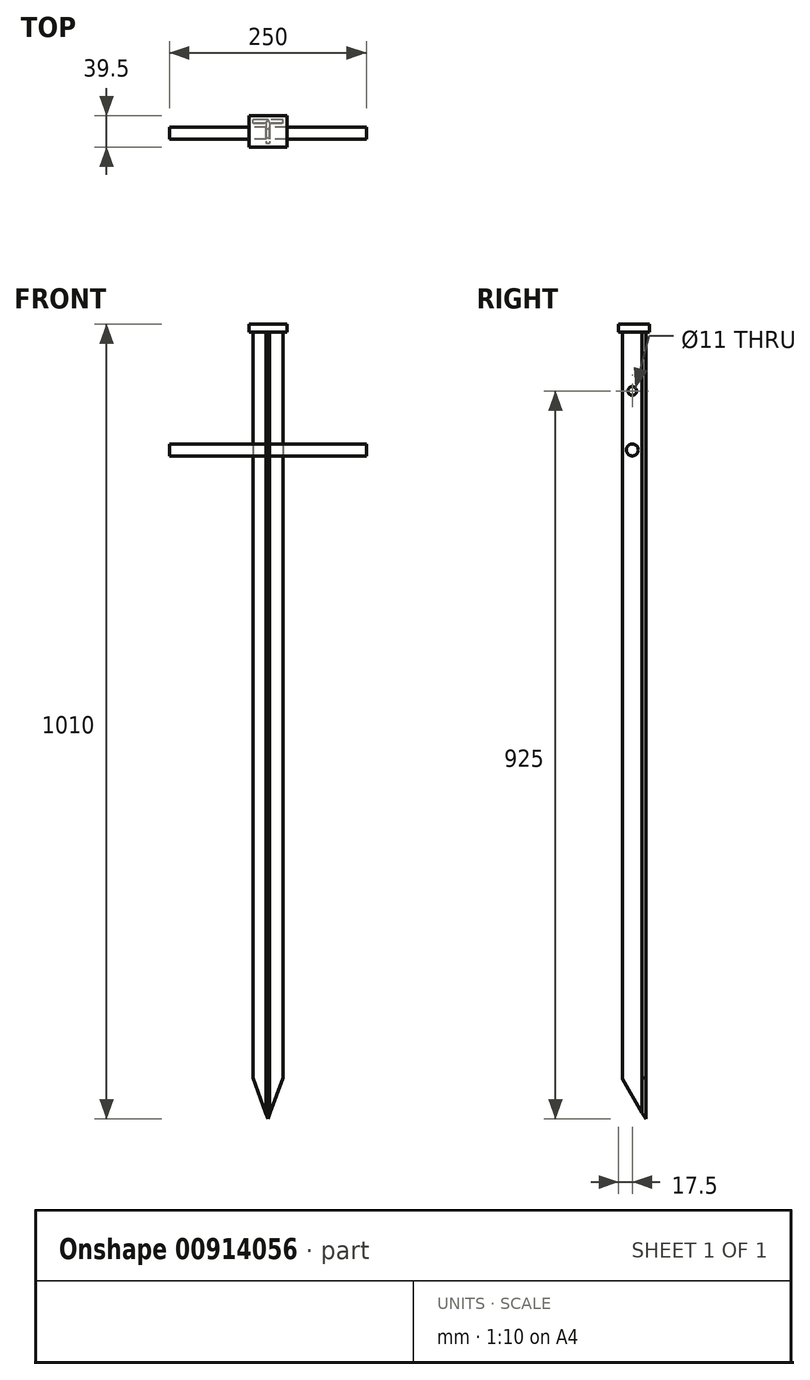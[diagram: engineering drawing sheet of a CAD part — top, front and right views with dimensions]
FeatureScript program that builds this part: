
annotation { "Feature Type Name" : "Feature", "Feature Type Description" : "" }
export const myFeature = defineFeature(function(context is Context, id is Id, definition is map)
    precondition{}
    {
        {
            var Q0;
            Q0=qCreatedBy(makeId("Top.planeOp"),FACE);
            var sketch = newSketch(context, id + "F0", { "sketchPlane" : qUnion([Q0])});
            skLineSegment(sketch, "E0.bottom", {"start": v(19, -2.25) * mm, "end": v(-19, -2.25) * mm});
            skLineSegment(sketch, "E0.top", {"start": v(19, 2.25) * mm, "end": v(-19, 2.25) * mm});
            skLineSegment(sketch, "E0.left", {"start": v(19, -2.25) * mm, "end": v(19, 2.25) * mm});
            skLineSegment(sketch, "E0.right", {"start": v(-19, -2.25) * mm, "end": v(-19, 2.25) * mm});
            skPoint(sketch, "E0.middle", {"position": v(0, 0) * mm});
            skLineSegment(sketch, "E1.bottom", {"start": v(2.25, -2.25) * mm, "end": v(-2.25, -2.25) * mm});
            skLineSegment(sketch, "E1.top", {"start": v(2.25, -27.25) * mm, "end": v(-2.25, -27.25) * mm});
            skLineSegment(sketch, "E1.left", {"start": v(2.25, -2.25) * mm, "end": v(2.25, -27.25) * mm});
            skLineSegment(sketch, "E1.right", {"start": v(-2.25, -2.25) * mm, "end": v(-2.25, -27.25) * mm});
            skPoint(sketch, "E1.middle", {"position": v(0, -14.75) * mm});
            skSolve(sketch);
        }
        {
            var Q0;
            Q0 = qSketchRegion(id + "F0", true);
            extrude(context, id + "F1", {"entities" : qUnion([Q0]), "depth" : 1000 * mm, "offsetDistance" : 25 * mm});
        }
        {
            var Q0;
            Q0=qCreatedBy(makeId("Right.planeOp"),FACE);
            var sketch = newSketch(context, id + "F2", { "sketchPlane" : qUnion([Q0])});
            skCircle(sketch, "E2", {"center": v(-14.75, 850) * mm, "radius": 7.5 * mm});
            skPoint(sketch, "E3", {"position": v(-14.75, 925) * mm});
            skLineSegment(sketch, "E4", {"start": v(-27.25, 925) * mm, "end": v(2.25, 925) * mm, "construction": true});
            skSolve(sketch);
        }
        {
            var Q0;
            Q0 = qSketchRegion(id + "F2", true);
            extrude(context, id + "F3", {"entities" : qUnion([Q0]), "operationType" : NewBodyOperationType.ADD, "endBound" : BoundingType.SYMMETRIC, "depth" : 250 * mm, "offsetDistance" : 25 * mm});
        }
        {
            var Q0;
            Q0=makeQuery(id+"F1.opExtrude","CAP_FACE",FACE,{"disambiguationData":[OSD([sQuery(id+"F0.wireOp",EDGE,"E0.bottom"),sQuery(id+"F0.wireOp",EDGE,"E0.top"),sQuery(id+"F0.wireOp",EDGE,"E0.left"),sQuery(id+"F0.wireOp",EDGE,"E0.right"),sQuery(id+"F0.wireOp",EDGE,"E1.top"),sQuery(id+"F0.wireOp",EDGE,"E1.left"),sQuery(id+"F0.wireOp",EDGE,"E1.right")])],"isStart":false});
            var sketch = newSketch(context, id + "F4", { "sketchPlane" : qUnion([Q0])});
            skLineSegment(sketch, "E5.bottom", {"start": v(-24, 7.25) * mm, "end": v(24, 7.25) * mm});
            skLineSegment(sketch, "E5.top", {"start": v(-24, -32.25) * mm, "end": v(24, -32.25) * mm});
            skLineSegment(sketch, "E5.left", {"start": v(-24, 7.25) * mm, "end": v(-24, -32.25) * mm});
            skLineSegment(sketch, "E5.right", {"start": v(24, 7.25) * mm, "end": v(24, -32.25) * mm});
            skSolve(sketch);
        }
        {
            var Q0;
            Q0 = qSketchRegion(id + "F4", true);
            extrude(context, id + "F5", {"entities" : qUnion([Q0]), "operationType" : NewBodyOperationType.ADD, "depth" : 10 * mm, "offsetDistance" : 25 * mm});
        }
        {
            var Q0;
            Q0=qCreatedBy(makeId("Right.planeOp"),FACE);
            var sketch = newSketch(context, id + "F6", { "sketchPlane" : qUnion([Q0])});
            skLineSegment(sketch, "E6", {"start": v(2.25, 0) * mm, "end": v(-27.25, 51.1) * mm});
            skLineSegment(sketch, "E7", {"start": v(2.25, 0) * mm, "end": v(-27.25, 0) * mm});
            skLineSegment(sketch, "E8", {"start": v(-27.25, 0) * mm, "end": v(-27.25, 51.1) * mm});
            skSolve(sketch);
        }
        {
            var Q0;
            Q0 = qSketchRegion(id + "F6", true);
            extrude(context, id + "F7", {"entities" : qUnion([Q0]), "operationType" : NewBodyOperationType.REMOVE, "endBound" : BoundingType.SYMMETRIC, "oppositeDirection" : true, "depth" : 100 * mm, "offsetDistance" : 25 * mm});
        }
        {
            var Q0;
            Q0=makeQuery(id+"F1.opExtrude","SWEPT_FACE",FACE,{"disambiguationData":[OSD([sQuery(id+"F0.wireOp",EDGE,"E0.top")])]});
            var sketch = newSketch(context, id + "F8", { "sketchPlane" : qUnion([Q0])});
            skLineSegment(sketch, "E9", {"start": v(0, 0) * mm, "end": v(19, 52.2) * mm});
            skLineSegment(sketch, "E10", {"start": v(-19, 52.2) * mm, "end": v(0, 0) * mm});
            skLineSegment(sketch, "E11", {"start": v(-19, 52.2) * mm, "end": v(-19, 0) * mm});
            skLineSegment(sketch, "E12", {"start": v(-19, 0) * mm, "end": v(19, 0) * mm});
            skLineSegment(sketch, "E13", {"start": v(19, 0) * mm, "end": v(19, 52.2) * mm});
            skSolve(sketch);
        }
        {
            var Q0;
            Q0 = qSketchRegion(id + "F8", true);
            extrude(context, id + "F9", {"entities" : qUnion([Q0]), "operationType" : NewBodyOperationType.REMOVE, "endBound" : BoundingType.THROUGH_ALL, "oppositeDirection" : true, "depth" : 25 * mm, "offsetDistance" : 25 * mm});
        }
        {
            var Q0;
            Q0=makeQuery(id+"F1.opExtrude","SWEPT_FACE",FACE,{"disambiguationData":[OSD([sQuery(id+"F0.wireOp",EDGE,"E1.left")])]});
            var sketch = newSketch(context, id + "F10", { "sketchPlane" : qUnion([Q0])});
            skPoint(sketch, "E14.0", {"position": v(-14.75, 925) * mm});
            skSolve(sketch);
        }
        {
            var Q0;
            Q0=sQuery(id+"F10.wireOp",VERTEX,"E14.0");
            var Q1;
            Q1=makeQuery(id+"F1.opExtrude","SWEPT_BODY",BODY,{"disambiguationData":[OSD([sQuery(id+"F0.wireOp",EDGE,"E0.bottom"),sQuery(id+"F0.wireOp",EDGE,"E0.top"),sQuery(id+"F0.wireOp",EDGE,"E0.left"),sQuery(id+"F0.wireOp",EDGE,"E0.right"),sQuery(id+"F0.wireOp",EDGE,"E1.top"),sQuery(id+"F0.wireOp",EDGE,"E1.left"),sQuery(id+"F0.wireOp",EDGE,"E1.right")])]});
            hole(context, id + "F11", {"style" : HoleStyle.SIMPLE, "endStyle" : HoleEndStyle.THROUGH, "standardTappedOrClearance" : lookupTablePath({ "fit" : "Normal", "standard" : "ISO", "size" : "M10", "type" : "Clearance" }), "standardBlindInLast" : lookupTablePath({ "fit" : "Normal", "standard" : "ISO", "size" : "M10", "type" : "Clearance" }), "holeDiameter" : 11 * mm, "majorDiameter" : 5 * mm, "isTappedThrough" : true, "tappedDepth" : 12 * mm, "tapClearance" : 3, "locations" : qUnion([Q0]), "scope" : qUnion([Q1])});
        }
    });
